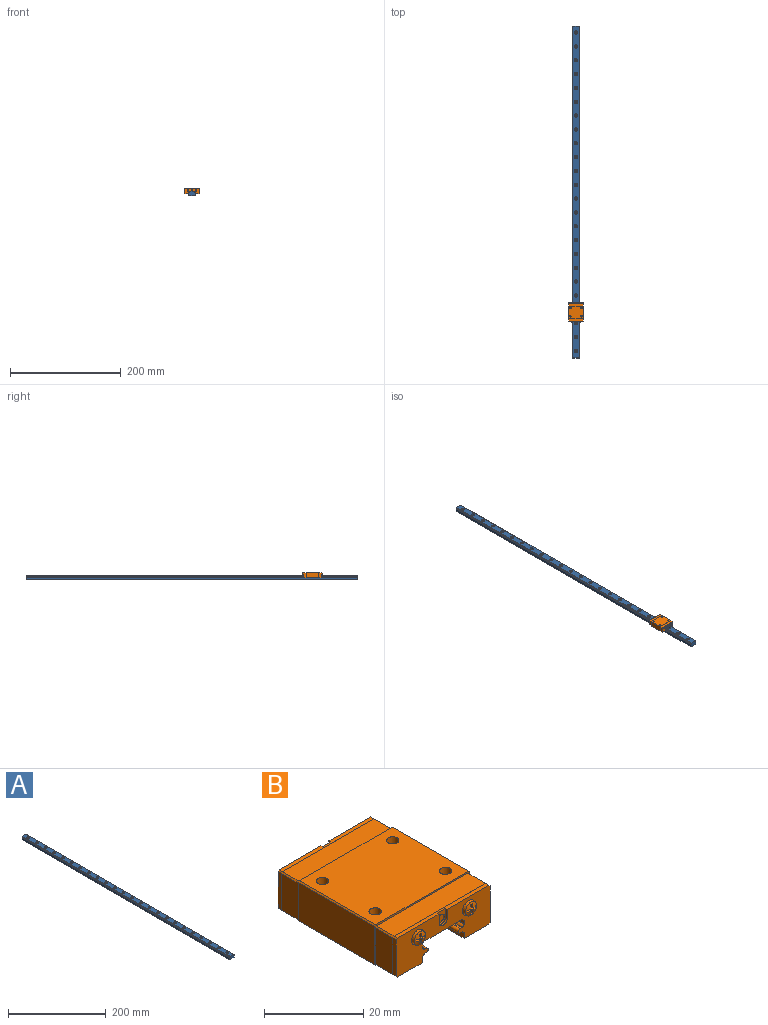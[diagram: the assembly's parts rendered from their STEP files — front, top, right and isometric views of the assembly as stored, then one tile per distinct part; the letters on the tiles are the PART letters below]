
ASSEMBLY  parts=2 mates=1
PART A: 100 faces, bbox 12x600x8 mm
  f0: cylinder r=1.75mm len=5mm, axis (0,0,1), area 55mm2, adj f25,f98
  f1: cylinder r=1.75mm len=5mm, axis (0,0,1), area 55mm2, adj f25,f96
  f2: cylinder r=1.75mm len=5mm, axis (0,0,1), area 55mm2, adj f25,f94
  f3: cylinder r=1.75mm len=5mm, axis (0,0,1), area 55mm2, adj f25,f92
  f4: cylinder r=1.75mm len=5mm, axis (0,0,1), area 55mm2, adj f25,f90
  f5: cylinder r=1.75mm len=5mm, axis (0,0,1), area 55mm2, adj f25,f88
  f6: cylinder r=1.75mm len=5mm, axis (0,0,1), area 55mm2, adj f25,f86
  f7: cylinder r=1.75mm len=5mm, axis (0,0,1), area 55mm2, adj f25,f84
  f8: cylinder r=1.75mm len=5mm, axis (0,0,1), area 55mm2, adj f25,f82
  f9: cylinder r=1.75mm len=5mm, axis (0,0,1), area 55mm2, adj f25,f80
  f10: cylinder r=1.75mm len=5mm, axis (0,0,1), area 55mm2, adj f25,f78
  f11: cylinder r=1.75mm len=5mm, axis (0,0,1), area 55mm2, adj f25,f76
  f12: cylinder r=1.75mm len=5mm, axis (0,0,1), area 55mm2, adj f25,f74
  f13: cylinder r=1.75mm len=5mm, axis (0,0,1), area 55mm2, adj f25,f72
  f14: cylinder r=1.75mm len=5mm, axis (0,0,1), area 55mm2, adj f25,f70
  f15: cylinder r=1.75mm len=5mm, axis (0,0,1), area 55mm2, adj f25,f68
  f16: cylinder r=1.75mm len=5mm, axis (0,0,1), area 55mm2, adj f25,f66
  f17: cylinder r=1.75mm len=5mm, axis (0,0,1), area 55mm2, adj f25,f64
  f18: cylinder r=1.75mm len=5mm, axis (0,0,1), area 55mm2, adj f25,f62
  f19: cylinder r=1.75mm len=5mm, axis (0,0,1), area 55mm2, adj f25,f60
  f20: cylinder r=1.75mm len=5mm, axis (0,0,1), area 55mm2, adj f25,f58
  f21: cylinder r=1.75mm len=5mm, axis (0,0,1), area 55mm2, adj f25,f56
  f22: cylinder r=1.75mm len=5mm, axis (0,0,1), area 55mm2, adj f25,f54
  f23: cylinder r=1.75mm len=5mm, axis (0,0,1), area 55mm2, adj f25,f52
  f24: plane 600x4.32mm, normal (-1,0,0), area 2593.1mm2, adj f25,f40,f41,f51
  f25: plane 600x12mm, normal (0,0,-1), area 6969.1mm2, adj f0,f1,f2,f3,f4,f5,f6,f7
  f26: plane 600x4.32mm, normal (1,0,0), area 2593.1mm2, adj f25,f40,f41,f44
  f27: cylinder r=1.14mm len=600mm, axis (0,1,0), area 375.6mm2, adj f40,f41,f44,f45
  f28: plane 600x0.42mm, normal (0,0,1), area 254.6mm2, adj f29,f40,f41,f45
  f29: cylinder r=0.5mm len=600mm, axis (0,1,0), area 1131.1mm2, adj f28,f30,f40,f41
  f30: plane 600x0.42mm, normal (0,0,-1), area 252.6mm2, adj f29,f40,f41,f46
  f31: cylinder r=1.14mm len=600mm, axis (0,1,0), area 376.1mm2, adj f40,f41,f46,f47
  f32: plane 600x0.91mm, normal (1,0,0), area 545.9mm2, adj f40,f41,f43,f47
  f33: plane 600x11mm, normal (0,0,1), area 5921.4mm2, adj f40,f41,f42,f43,f53,f55,f57,f59
  f34: plane 600x0.91mm, normal (-1,0,0), area 545.9mm2, adj f40,f41,f42,f48
  f35: cylinder r=1.14mm len=600mm, axis (0,1,0), area 376.1mm2, adj f40,f41,f48,f49
  f36: plane 600x0.42mm, normal (0,0,-1), area 252.6mm2, adj f37,f40,f41,f49
  f37: cylinder r=0.5mm len=600mm, axis (0,1,0), area 1131.1mm2, adj f36,f38,f40,f41
  f38: plane 600x0.42mm, normal (0,0,1), area 254.6mm2, adj f37,f40,f41,f50
  f39: cylinder r=1.14mm len=600mm, axis (0,1,0), area 375.6mm2, adj f40,f41,f50,f51
  f40: plane 12x8mm, normal (0,-1,0), area 91.8mm2, adj f24,f25,f26,f27,f28,f29,f30,f31
  f41: plane 12x8mm, normal (0,1,0), area 91.8mm2, adj f24,f25,f26,f27,f28,f29,f30,f31
  f42: plane 600x0.5mm, normal (-0.71,0,0.71), area 424.3mm2, adj f33,f34,f40,f41
  f43: plane 600x0.5mm, normal (0.71,0,0.71), area 424.3mm2, adj f32,f33,f40,f41
  f44: cylinder r=0.16mm len=600mm, axis (0,1,0), area 101.8mm2, adj f26,f27,f40,f41
  f45: cylinder r=0.16mm len=600mm, axis (0,1,0), area 101.7mm2, adj f27,f28,f40,f41
  f46: cylinder r=0.16mm len=600mm, axis (0,1,0), area 101.8mm2, adj f30,f31,f40,f41
  f47: cylinder r=0.16mm len=600mm, axis (0,1,0), area 101.8mm2, adj f31,f32,f40,f41
  f48: cylinder r=0.16mm len=600mm, axis (0,1,0), area 101.8mm2, adj f34,f35,f40,f41
  f49: cylinder r=0.16mm len=600mm, axis (0,1,0), area 101.8mm2, adj f35,f36,f40,f41
  f50: cylinder r=0.16mm len=600mm, axis (0,1,0), area 101.7mm2, adj f38,f39,f40,f41
  f51: cylinder r=0.16mm len=600mm, axis (0,1,0), area 101.8mm2, adj f24,f39,f40,f41
  f52: plane 6x6mm, normal (0,0,1), area 18.7mm2, adj f23,f53
  f53: cylinder r=3mm len=6mm, axis (0,0,1), area 56.5mm2, adj f33,f52
  f54: plane 6x6mm, normal (0,0,1), area 18.7mm2, adj f22,f55
  f55: cylinder r=3mm len=6mm, axis (0,0,1), area 56.5mm2, adj f33,f54
  f56: plane 6x6mm, normal (0,0,1), area 18.7mm2, adj f21,f57
  f57: cylinder r=3mm len=6mm, axis (0,0,1), area 56.5mm2, adj f33,f56
  f58: plane 6x6mm, normal (0,0,1), area 18.7mm2, adj f20,f59
  f59: cylinder r=3mm len=6mm, axis (0,0,1), area 56.5mm2, adj f33,f58
  f60: plane 6x6mm, normal (0,0,1), area 18.7mm2, adj f19,f61
  f61: cylinder r=3mm len=6mm, axis (0,0,1), area 56.5mm2, adj f33,f60
  f62: plane 6x6mm, normal (0,0,1), area 18.7mm2, adj f18,f63
  f63: cylinder r=3mm len=6mm, axis (0,0,1), area 56.5mm2, adj f33,f62
  f64: plane 6x6mm, normal (0,0,1), area 18.7mm2, adj f17,f65
  f65: cylinder r=3mm len=6mm, axis (0,0,1), area 56.5mm2, adj f33,f64
  f66: plane 6x6mm, normal (0,0,1), area 18.7mm2, adj f16,f67
  f67: cylinder r=3mm len=6mm, axis (0,0,1), area 56.5mm2, adj f33,f66
  f68: plane 6x6mm, normal (0,0,1), area 18.7mm2, adj f15,f69
  f69: cylinder r=3mm len=6mm, axis (0,0,1), area 56.5mm2, adj f33,f68
  f70: plane 6x6mm, normal (0,0,1), area 18.7mm2, adj f14,f71
  f71: cylinder r=3mm len=6mm, axis (0,0,1), area 56.5mm2, adj f33,f70
  f72: plane 6x6mm, normal (0,0,1), area 18.7mm2, adj f13,f73
  f73: cylinder r=3mm len=6mm, axis (0,0,1), area 56.5mm2, adj f33,f72
  f74: plane 6x6mm, normal (0,0,1), area 18.7mm2, adj f12,f75
  f75: cylinder r=3mm len=6mm, axis (0,0,1), area 56.5mm2, adj f33,f74
  f76: plane 6x6mm, normal (0,0,1), area 18.7mm2, adj f11,f77
  f77: cylinder r=3mm len=6mm, axis (0,0,1), area 56.5mm2, adj f33,f76
  f78: plane 6x6mm, normal (0,0,1), area 18.7mm2, adj f10,f79
  f79: cylinder r=3mm len=6mm, axis (0,0,1), area 56.5mm2, adj f33,f78
  f80: plane 6x6mm, normal (0,0,1), area 18.7mm2, adj f9,f81
  f81: cylinder r=3mm len=6mm, axis (0,0,1), area 56.5mm2, adj f33,f80
  f82: plane 6x6mm, normal (0,0,1), area 18.7mm2, adj f8,f83
  f83: cylinder r=3mm len=6mm, axis (0,0,1), area 56.5mm2, adj f33,f82
  f84: plane 6x6mm, normal (0,0,1), area 18.7mm2, adj f7,f85
  f85: cylinder r=3mm len=6mm, axis (0,0,1), area 56.5mm2, adj f33,f84
  f86: plane 6x6mm, normal (0,0,1), area 18.7mm2, adj f6,f87
  f87: cylinder r=3mm len=6mm, axis (0,0,1), area 56.5mm2, adj f33,f86
  f88: plane 6x6mm, normal (0,0,1), area 18.7mm2, adj f5,f89
  f89: cylinder r=3mm len=6mm, axis (0,0,1), area 56.5mm2, adj f33,f88
  f90: plane 6x6mm, normal (0,0,1), area 18.7mm2, adj f4,f91
  f91: cylinder r=3mm len=6mm, axis (0,0,1), area 56.5mm2, adj f33,f90
  f92: plane 6x6mm, normal (0,0,1), area 18.7mm2, adj f3,f93
  f93: cylinder r=3mm len=6mm, axis (0,0,1), area 56.5mm2, adj f33,f92
  f94: plane 6x6mm, normal (0,0,1), area 18.7mm2, adj f2,f95
  f95: cylinder r=3mm len=6mm, axis (0,0,1), area 56.5mm2, adj f33,f94
  f96: plane 6x6mm, normal (0,0,1), area 18.7mm2, adj f1,f97
  f97: cylinder r=3mm len=6mm, axis (0,0,1), area 56.5mm2, adj f33,f96
  f98: plane 6x6mm, normal (0,0,1), area 18.7mm2, adj f0,f99
  f99: cylinder r=3mm len=6mm, axis (0,0,1), area 56.5mm2, adj f33,f98
PART B: 172 faces, bbox 27x35.9x10 mm
  f0: cylinder r=1.25mm len=3.5mm, axis (0,0,-1), area 27.5mm2, adj f1,f158
  f1: cone r=0.62mm half-angle=59deg, axis (0,0,1), area 5.7mm2, adj f0
  f2: cylinder r=1.25mm len=3.5mm, axis (0,0,-1), area 27.5mm2, adj f3,f158
  f3: cone r=0.62mm half-angle=59deg, axis (0,0,1), area 5.7mm2, adj f2
  f4: cylinder r=1.25mm len=3.5mm, axis (0,0,-1), area 27.5mm2, adj f5,f158
  f5: cone r=0.62mm half-angle=59deg, axis (0,0,1), area 5.7mm2, adj f4
  f6: cylinder r=1.25mm len=3.5mm, axis (0,0,-1), area 27.5mm2, adj f7,f158
  f7: cone r=0.62mm half-angle=59deg, axis (0,0,1), area 5.7mm2, adj f6
  f8: cylinder r=0.5mm len=33.7mm, axis (0,1,0), area 63.6mm2, adj f58,f115,f148,f149
  f9: cylinder r=0.5mm len=33.7mm, axis (0,1,0), area 63.6mm2, adj f58,f115,f137,f138
  f10: cylinder r=1.15mm len=2.3mm, axis (0,1,0), area 3.6mm2, adj f114,f124
  f11: cylinder r=1.75mm len=3.5mm, axis (0,1,0), area 5.5mm2, adj f109,f115
  f12: cylinder r=1.75mm len=3.5mm, axis (0,1,0), area 5.5mm2, adj f108,f115
  f13: cone r=0.85mm half-angle=5deg, axis (0,1,0), area 11.5mm2, adj f14,f109
  f14: cone r=0.8mm half-angle=72.7deg, axis (0,1,0), area 6.3mm2, adj f13,f96,f97,f98,f99,f100,f101,f102
  f15: cone r=0.85mm half-angle=5deg, axis (0,1,0), area 11.5mm2, adj f16,f108
  f16: cone r=0.8mm half-angle=72.7deg, axis (0,1,0), area 6.3mm2, adj f15,f83,f84,f85,f86,f87,f88,f89
  f17: cylinder r=1.15mm len=2.3mm, axis (0,-1,0), area 3.6mm2, adj f57,f67
  f18: cylinder r=1.75mm len=3.5mm, axis (0,-1,0), area 5.5mm2, adj f52,f58
  f19: cylinder r=1.75mm len=3.5mm, axis (0,-1,0), area 5.5mm2, adj f51,f58
  f20: cone r=0.85mm half-angle=5deg, axis (0,-1,0), area 11.5mm2, adj f21,f52
  f21: cone r=0.8mm half-angle=72.7deg, axis (0,-1,0), area 6.3mm2, adj f20,f39,f40,f41,f42,f43,f44,f45
  f22: cone r=0.85mm half-angle=5deg, axis (0,-1,0), area 11.5mm2, adj f23,f51
  f23: cone r=0.8mm half-angle=72.7deg, axis (0,-1,0), area 6.3mm2, adj f22,f26,f27,f28,f29,f30,f31,f32
  f24: plane 26.6x9.6mm, normal (0,-1,0), area 0.3mm2, adj f55,f59,f60,f61,f62,f63,f64,f65
  f25: plane 2.4x2.4mm, normal (0,1,0), area 2.1mm2, adj f26,f27,f28,f29,f30,f31,f32,f33
  f26: plane 0.93x0.49mm, normal (0,0,1), area 0.4mm2, adj f23,f25,f29,f31
  f27: plane 0.93x0.49mm, normal (0,0,-1), area 0.4mm2, adj f23,f25,f28,f30
  f28: plane 1.36x1.29mm, normal (-1,0,0), area 1mm2, adj f23,f25,f27,f36
  f29: plane 1.36x1.29mm, normal (-1,0,0), area 1mm2, adj f23,f25,f26,f32
  f30: plane 1.36x1.29mm, normal (1,0,0), area 1mm2, adj f23,f25,f27,f33
  f31: plane 1.36x1.29mm, normal (1,0,0), area 1mm2, adj f23,f25,f26,f34
  f32: plane 1.36x1.29mm, normal (0,0,1), area 1mm2, adj f23,f25,f29,f35
  f33: plane 1.36x1.29mm, normal (0,0,-1), area 1mm2, adj f23,f25,f30,f37
  f34: plane 1.36x1.29mm, normal (0,0,1), area 1mm2, adj f23,f25,f31,f37
  f35: plane 0.93x0.49mm, normal (-1,0,0), area 0.4mm2, adj f23,f25,f32,f36
  f36: plane 1.36x1.29mm, normal (0,0,-1), area 1mm2, adj f23,f25,f28,f35
  f37: plane 0.94x0.49mm, normal (1,0,0), area 0.4mm2, adj f23,f25,f33,f34
  f38: plane 2.4x2.4mm, normal (0,1,0), area 2.1mm2, adj f39,f40,f41,f42,f43,f44,f45,f46
  f39: plane 0.93x0.49mm, normal (0,0,1), area 0.4mm2, adj f21,f38,f42,f44
  f40: plane 0.93x0.49mm, normal (0,0,-1), area 0.4mm2, adj f21,f38,f41,f43
  f41: plane 1.36x1.29mm, normal (-1,0,0), area 1mm2, adj f21,f38,f40,f49
  f42: plane 1.36x1.29mm, normal (-1,0,0), area 1mm2, adj f21,f38,f39,f45
  f43: plane 1.36x1.29mm, normal (1,0,0), area 1mm2, adj f21,f38,f40,f46
  f44: plane 1.36x1.29mm, normal (1,0,0), area 1mm2, adj f21,f38,f39,f47
  f45: plane 1.36x1.29mm, normal (0,0,1), area 1mm2, adj f21,f38,f42,f48
  f46: plane 1.36x1.29mm, normal (0,0,-1), area 1mm2, adj f21,f38,f43,f50
  f47: plane 1.36x1.29mm, normal (0,0,1), area 1mm2, adj f21,f38,f44,f50
  f48: plane 0.93x0.49mm, normal (-1,0,0), area 0.4mm2, adj f21,f38,f45,f49
  f49: plane 1.36x1.29mm, normal (0,0,-1), area 1mm2, adj f21,f38,f41,f48
  f50: plane 0.94x0.49mm, normal (1,0,0), area 0.4mm2, adj f21,f38,f46,f47
  f51: plane 3.5x3.5mm, normal (0,1,0), area 0.5mm2, adj f19,f22
  f52: plane 3.5x3.5mm, normal (0,1,0), area 0.5mm2, adj f18,f20
  f53: plane 2.1x0.5mm, normal (1,0,0), area 1.1mm2, adj f55,f56,f57,f58
  f54: plane 2.1x0.5mm, normal (-1,0,0), area 1.1mm2, adj f55,f56,f57,f58
  f55: plane 26x1mm, normal (0,0,1), area 24.8mm2, adj f24,f53,f54,f57,f58,f62,f63
  f56: cylinder r=1.2mm len=2.4mm, axis (0,-1,0), area 1.9mm2, adj f53,f54,f57,f58
  f57: plane 3.3x2.4mm, normal (0,1,0), area 3.1mm2, adj f17,f53,f54,f55,f56
  f58: plane 26.6x9.6mm, normal (0,1,0), area 172.9mm2, adj f8,f9,f18,f19,f53,f54,f55,f56
  f59: plane 7x1mm, normal (0,0,-1), area 7mm2, adj f24,f58,f65,f134
  f60: plane 7x1mm, normal (0,0,-1), area 7mm2, adj f24,f58,f66,f152
  f61: plane 9x1mm, normal (1,0,0), area 9mm2, adj f24,f58,f62,f66
  f62: plane 1x0.3mm, normal (0.71,0,0.71), area 0.4mm2, adj f24,f55,f58,f61
  f63: plane 1x0.3mm, normal (-0.71,0,0.71), area 0.4mm2, adj f24,f55,f58,f64
  f64: plane 9x1mm, normal (-1,0,0), area 9mm2, adj f24,f58,f63,f65
  f65: plane 1x0.3mm, normal (-0.71,0,-0.71), area 0.4mm2, adj f24,f58,f59,f64
  f66: plane 1x0.3mm, normal (0.71,0,-0.71), area 0.4mm2, adj f24,f58,f60,f61
  f67: plane 2.3x2.3mm, normal (0,1,0), area 4.2mm2, adj f17
  f68: cylinder r=1.14mm len=33.7mm, axis (0,-1,0), area 21.1mm2, adj f58,f115,f150,f151
  f69: cylinder r=1.14mm len=33.7mm, axis (0,-1,0), area 21.1mm2, adj f58,f115,f146,f147
  f70: cylinder r=1.14mm len=33.7mm, axis (0,-1,0), area 21.1mm2, adj f58,f115,f139,f140
  f71: cylinder r=1.14mm len=33.7mm, axis (0,-1,0), area 21.1mm2, adj f58,f115,f135,f136
  f72: plane 7x5mm, normal (0,0,-1), area 35mm2, adj f24,f79,f134,f163
  f73: plane 7x5mm, normal (0,0,-1), area 35mm2, adj f24,f80,f152,f163
  f74: plane 8.99x5mm, normal (1,0,0), area 45mm2, adj f24,f75,f80,f163
  f75: plane 5x0.3mm, normal (0.71,0,0.71), area 2.1mm2, adj f24,f74,f76,f163
  f76: plane 25.99x5mm, normal (0,0,1), area 130mm2, adj f24,f75,f77,f163
  f77: plane 5x0.3mm, normal (-0.71,0,0.71), area 2.1mm2, adj f24,f76,f78,f163
  f78: plane 8.99x5mm, normal (-1,0,0), area 45mm2, adj f24,f77,f79,f163
  f79: plane 5x0.3mm, normal (-0.71,0,-0.71), area 2.1mm2, adj f24,f72,f78,f163
  f80: plane 5x0.3mm, normal (0.71,0,-0.71), area 2.1mm2, adj f24,f73,f74,f163
  f81: plane 26.6x9.6mm, normal (0,1,0), area 0.3mm2, adj f112,f116,f117,f118,f119,f120,f121,f122
  f82: plane 2.4x2.4mm, normal (0,-1,0), area 2.1mm2, adj f83,f84,f85,f86,f87,f88,f89,f90
  f83: plane 0.93x0.49mm, normal (0,0,1), area 0.4mm2, adj f16,f82,f86,f88
  f84: plane 0.93x0.49mm, normal (0,0,-1), area 0.4mm2, adj f16,f82,f85,f87
  f85: plane 1.36x1.29mm, normal (1,0,0), area 1mm2, adj f16,f82,f84,f93
  f86: plane 1.36x1.29mm, normal (1,0,0), area 1mm2, adj f16,f82,f83,f89
  f87: plane 1.36x1.29mm, normal (-1,0,0), area 1mm2, adj f16,f82,f84,f90
  f88: plane 1.36x1.29mm, normal (-1,0,0), area 1mm2, adj f16,f82,f83,f91
  f89: plane 1.36x1.29mm, normal (0,0,1), area 1mm2, adj f16,f82,f86,f92
  f90: plane 1.36x1.29mm, normal (0,0,-1), area 1mm2, adj f16,f82,f87,f94
  f91: plane 1.36x1.29mm, normal (0,0,1), area 1mm2, adj f16,f82,f88,f94
  f92: plane 0.93x0.49mm, normal (1,0,0), area 0.4mm2, adj f16,f82,f89,f93
  f93: plane 1.36x1.29mm, normal (0,0,-1), area 1mm2, adj f16,f82,f85,f92
  f94: plane 0.94x0.49mm, normal (-1,0,0), area 0.4mm2, adj f16,f82,f90,f91
  f95: plane 2.4x2.4mm, normal (0,-1,0), area 2.1mm2, adj f96,f97,f98,f99,f100,f101,f102,f103
  f96: plane 0.93x0.49mm, normal (0,0,1), area 0.4mm2, adj f14,f95,f99,f101
  f97: plane 0.93x0.49mm, normal (0,0,-1), area 0.4mm2, adj f14,f95,f98,f100
  f98: plane 1.36x1.29mm, normal (1,0,0), area 1mm2, adj f14,f95,f97,f106
  f99: plane 1.36x1.29mm, normal (1,0,0), area 1mm2, adj f14,f95,f96,f102
  f100: plane 1.36x1.29mm, normal (-1,0,0), area 1mm2, adj f14,f95,f97,f103
  f101: plane 1.36x1.29mm, normal (-1,0,0), area 1mm2, adj f14,f95,f96,f104
  f102: plane 1.36x1.29mm, normal (0,0,1), area 1mm2, adj f14,f95,f99,f105
  f103: plane 1.36x1.29mm, normal (0,0,-1), area 1mm2, adj f14,f95,f100,f107
  f104: plane 1.36x1.29mm, normal (0,0,1), area 1mm2, adj f14,f95,f101,f107
  f105: plane 0.93x0.49mm, normal (1,0,0), area 0.4mm2, adj f14,f95,f102,f106
  f106: plane 1.36x1.29mm, normal (0,0,-1), area 1mm2, adj f14,f95,f98,f105
  f107: plane 0.94x0.49mm, normal (-1,0,0), area 0.4mm2, adj f14,f95,f103,f104
  f108: plane 3.5x3.5mm, normal (0,-1,0), area 0.5mm2, adj f12,f15
  f109: plane 3.5x3.5mm, normal (0,-1,0), area 0.5mm2, adj f11,f13
  f110: plane 2.1x0.5mm, normal (-1,0,0), area 1mm2, adj f112,f113,f114,f115
  f111: plane 2.1x0.5mm, normal (1,0,0), area 1mm2, adj f112,f113,f114,f115
  f112: plane 26x1mm, normal (0,0,1), area 24.8mm2, adj f81,f110,f111,f114,f115,f119,f120
  f113: cylinder r=1.2mm len=2.4mm, axis (0,1,0), area 1.9mm2, adj f110,f111,f114,f115
  f114: plane 3.3x2.4mm, normal (0,-1,0), area 3.1mm2, adj f10,f110,f111,f112,f113
  f115: plane 26.6x9.6mm, normal (0,-1,0), area 172.9mm2, adj f8,f9,f11,f12,f68,f69,f70,f71
  f116: plane 7x1mm, normal (0,0,-1), area 7mm2, adj f81,f115,f122,f152
  f117: plane 7x1mm, normal (0,0,-1), area 7mm2, adj f81,f115,f123,f134
  f118: plane 9x1mm, normal (-1,0,0), area 9mm2, adj f81,f115,f119,f123
  f119: plane 1x0.3mm, normal (-0.71,0,0.71), area 0.4mm2, adj f81,f112,f115,f118
  f120: plane 1x0.3mm, normal (0.71,0,0.71), area 0.4mm2, adj f81,f112,f115,f121
  f121: plane 9x1mm, normal (1,0,0), area 9mm2, adj f81,f115,f120,f122
  f122: plane 1x0.3mm, normal (0.71,0,-0.71), area 0.4mm2, adj f81,f115,f116,f121
  f123: plane 1x0.3mm, normal (-0.71,0,-0.71), area 0.4mm2, adj f81,f115,f117,f118
  f124: plane 2.3x2.3mm, normal (0,-1,0), area 4.2mm2, adj f10
  f125: plane 7x5mm, normal (0,0,-1), area 35mm2, adj f81,f132,f152,f153
  f126: plane 7x5mm, normal (0,0,-1), area 35mm2, adj f81,f133,f134,f153
  f127: plane 8.99x5mm, normal (-1,0,0), area 44.9mm2, adj f81,f128,f133,f153
  f128: plane 5x0.3mm, normal (-0.71,0,0.71), area 2.1mm2, adj f81,f127,f129,f153
  f129: plane 25.99x5mm, normal (0,0,1), area 129.9mm2, adj f81,f128,f130,f153
  f130: plane 5x0.3mm, normal (0.71,0,0.71), area 2.1mm2, adj f81,f129,f131,f153
  f131: plane 8.99x5mm, normal (1,0,0), area 45mm2, adj f81,f130,f132,f153
  f132: plane 5x0.3mm, normal (0.71,0,-0.71), area 2.1mm2, adj f81,f125,f131,f153
  f133: plane 5x0.3mm, normal (-0.71,0,-0.71), area 2.1mm2, adj f81,f126,f127,f153
  f134: plane 33.7x1.32mm, normal (1,0,0), area 44.5mm2, adj f24,f58,f59,f72,f81,f115,f117,f126
  f135: cylinder r=0.16mm len=33.7mm, axis (0,1,0), area 5.7mm2, adj f58,f71,f115,f134
  f136: cylinder r=0.16mm len=33.7mm, axis (0,1,0), area 5.7mm2, adj f58,f71,f115,f137
  f137: plane 33.7x0.42mm, normal (0,0,-1), area 14.2mm2, adj f9,f58,f115,f136
  f138: plane 33.7x0.42mm, normal (0,0,1), area 14.2mm2, adj f9,f58,f115,f139
  f139: cylinder r=0.16mm len=33.7mm, axis (0,1,0), area 5.7mm2, adj f58,f70,f115,f138
  f140: cylinder r=0.16mm len=33.7mm, axis (0,1,0), area 5.7mm2, adj f58,f70,f115,f141
  f141: plane 33.7x0.82mm, normal (1,0,0), area 27.7mm2, adj f58,f115,f140,f142
  f142: plane 33.7x0.59mm, normal (0.76,0,-0.65), area 26mm2, adj f58,f115,f141,f143
  f143: plane 33.7x11mm, normal (0,0,-1), area 370.7mm2, adj f58,f115,f142,f144
  f144: plane 33.7x0.59mm, normal (-0.76,0,-0.65), area 26mm2, adj f58,f115,f143,f145
  f145: plane 33.7x0.82mm, normal (-1,0,0), area 27.7mm2, adj f58,f115,f144,f146
  f146: cylinder r=0.16mm len=33.7mm, axis (0,1,0), area 5.7mm2, adj f58,f69,f115,f145
  f147: cylinder r=0.16mm len=33.7mm, axis (0,1,0), area 5.7mm2, adj f58,f69,f115,f148
  f148: plane 33.7x0.42mm, normal (0,0,1), area 14.2mm2, adj f8,f58,f115,f147
  f149: plane 33.7x0.42mm, normal (0,0,-1), area 14.2mm2, adj f8,f58,f115,f150
  f150: cylinder r=0.16mm len=33.7mm, axis (0,1,0), area 5.7mm2, adj f58,f68,f115,f149
  f151: cylinder r=0.16mm len=33.7mm, axis (0,1,0), area 5.7mm2, adj f58,f68,f115,f152
  f152: plane 33.7x1.32mm, normal (-1,0,0), area 44.5mm2, adj f24,f58,f60,f73,f81,f115,f116,f125
  f153: plane 27x10mm, normal (0,-1,0), area 14.9mm2, adj f125,f126,f127,f128,f129,f130,f131,f132
  f154: plane 21.7x7.2mm, normal (0,0,-1), area 156.2mm2, adj f152,f153,f161,f163
  f155: plane 21.7x7.2mm, normal (0,0,-1), area 156.2mm2, adj f134,f153,f162,f163
  f156: plane 21.7x9.4mm, normal (-1,0,0), area 204mm2, adj f153,f157,f162,f163
  f157: plane 21.7x0.3mm, normal (-0.71,0,0.71), area 9.2mm2, adj f153,f156,f158,f163
  f158: plane 26.4x21.7mm, normal (0,0,1), area 553.2mm2, adj f0,f2,f4,f6,f153,f157,f159,f163
  f159: plane 21.7x0.3mm, normal (0.71,0,0.71), area 9.2mm2, adj f153,f158,f160,f163
  f160: plane 21.7x9.4mm, normal (1,0,0), area 204mm2, adj f153,f159,f161,f163
  f161: plane 21.7x0.3mm, normal (0.71,0,-0.71), area 9.2mm2, adj f153,f154,f160,f163
  f162: plane 21.7x0.3mm, normal (-0.71,0,-0.71), area 9.2mm2, adj f153,f155,f156,f163
  f163: plane 27x10mm, normal (0,1,0), area 14.9mm2, adj f72,f73,f74,f75,f76,f77,f78,f79
  f164: cone r=0.5mm half-angle=17.1deg, axis (0,-1,0), area 2.7mm2, adj f166,f167
  f165: cylinder r=1.25mm len=2.5mm, axis (0,-1,0), area 3.9mm2, adj f166,f167
  f166: plane 2.5x2.5mm, normal (0,1,0), area 2.3mm2, adj f164,f165
  f167: plane 2.5x2.5mm, normal (0,-1,0), area 3.1mm2, adj f164,f165
  f168: cylinder r=1.25mm len=2.5mm, axis (0,-1,0), area 3.9mm2, adj f170,f171
  f169: cone r=0.5mm half-angle=17.1deg, axis (0,-1,0), area 2.7mm2, adj f170,f171
  f170: plane 2.5x2.5mm, normal (0,-1,0), area 3.1mm2, adj f168,f169
  f171: plane 2.5x2.5mm, normal (0,1,0), area 2.3mm2, adj f168,f169
PLACE A t=(-199.02,610.43,213.47)mm
PLACE B t=(-205.02,76.18,213.47)mm
MATE slider A.f29 <-> B.f8  axis (0,-1,0) through (-200.25,10.43,218.93)mm
